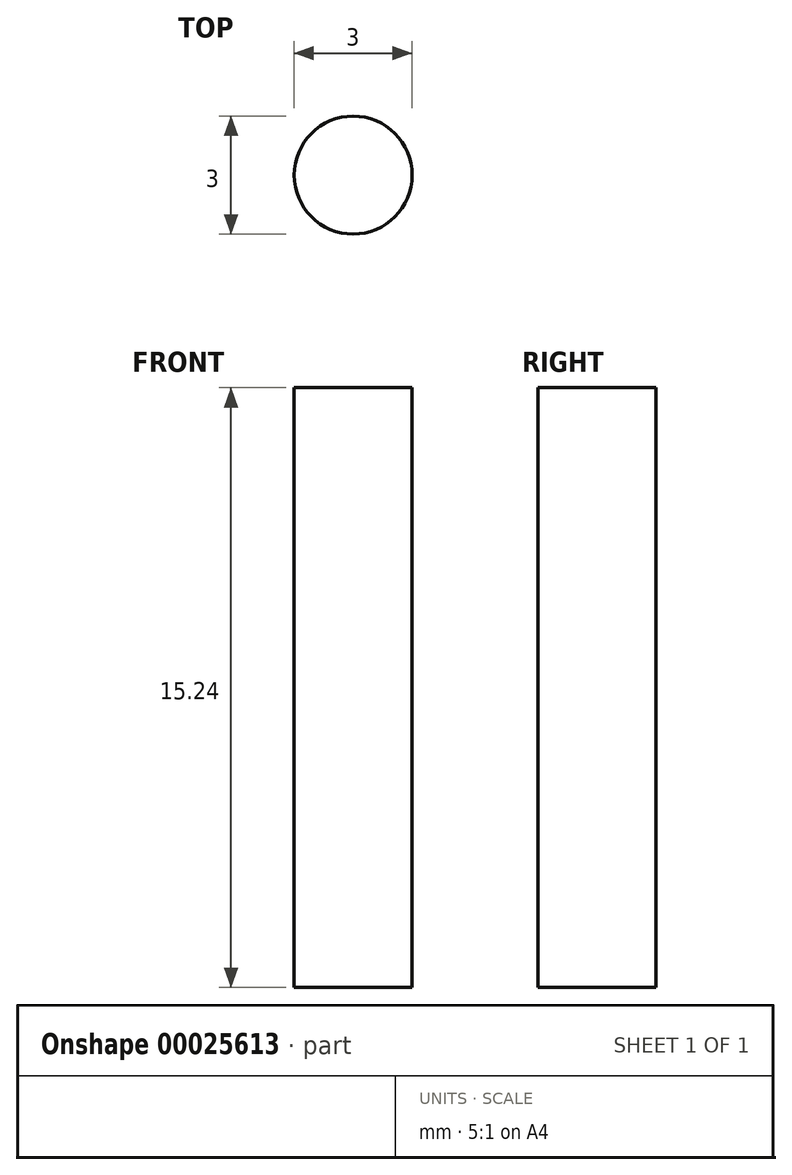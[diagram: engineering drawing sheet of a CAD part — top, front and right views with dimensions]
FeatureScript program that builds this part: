
annotation { "Feature Type Name" : "Feature", "Feature Type Description" : "" }
export const myFeature = defineFeature(function(context is Context, id is Id, definition is map)
    precondition{}
    {
        {
            var Q0;
            Q0=qCreatedBy(makeId("Front.planeOp"),FACE);
            var sketch = newSketch(context, id + "F0", { "sketchPlane" : qUnion([Q0])});
            skLineSegment(sketch, "E0", {"start": v(-10.74, 4.65) * mm, "end": v(-10.74, -10.6) * mm});
            skLineSegment(sketch, "E1", {"start": v(-10.74, -10.6) * mm, "end": v(-7.74, -10.6) * mm});
            skLineSegment(sketch, "E2", {"start": v(-7.74, -10.6) * mm, "end": v(-7.74, 4.65) * mm});
            skLineSegment(sketch, "E3", {"start": v(-7.74, 4.65) * mm, "end": v(-10.74, 4.65) * mm});
            skLineSegment(sketch, "E4", {"start": v(-9.24, 4.65) * mm, "end": v(-9.24, -10.6) * mm});
            skSolve(sketch);
        }
        {
            var Q0;
            {var subQ2=sQuery(id+"F0.wireOp",EDGE,"E2");Q0=makeQuery(id+"F0.imprint","IMPRINT",FACE,{"disambiguationData":[TD([[makeQuery(id+"F0.imprint","IMPRINT",EDGE,{"derivedFrom":subQ2}),1.0]])]});}
            var Q1;
            Q1=sQuery(id+"F0.wireOp",EDGE,"E4");
            revolve(context, id + "F1", {"entities" : qUnion([Q0]), "axis" : qUnion([Q1]), "revolveType" : RevolveType.FULL});
        }
    });
